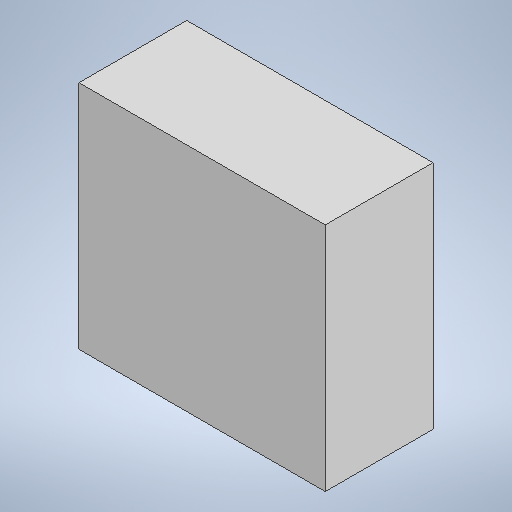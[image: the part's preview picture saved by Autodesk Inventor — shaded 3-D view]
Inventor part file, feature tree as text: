
AUTODESK INVENTOR PART (.ipt)
format: ipt  version: 2025.2 (Build 292293000, 293)  size: 234,496 bytes
history: native  units: mm
features: extrude x4, sketch x4
ambient origin geometry x8: Origin, YZ Plane, XZ Plane, XY Plane, X Axis, Y Axis, Z Axis, Center Point
bodies: Solid1 (feature_tree)
feature tree (8):
  extrude  "Extrusion1"  Depth=101.6mm
  extrude  "Extrusion2"  Depth=76.2mm
  extrude  "Extrusion3"  Depth=50.8mm
  extrude  "Extrusion4"  Depth=5.0mm TaperAngle=0.0deg
  sketch  "Sketch1"  dims[d0=95.25mm d1=101.6mm]
  sketch  "Sketch2"  dims[d2=44.45mm d3=0.0mm d4=76.2mm]
  sketch  "Sketch3"  dims[d5=50.8mm d6=8.0mm]
  sketch  "Sketch4"  dims[d7=15.0mm d8=5.0mm d9=0.0mm d10=12.192mm d11=25.0mm d12=1.27mm d13=0.0mm d14=25.0mm d15=9.128125mm d16=15.24mm d17=0.0mm]
